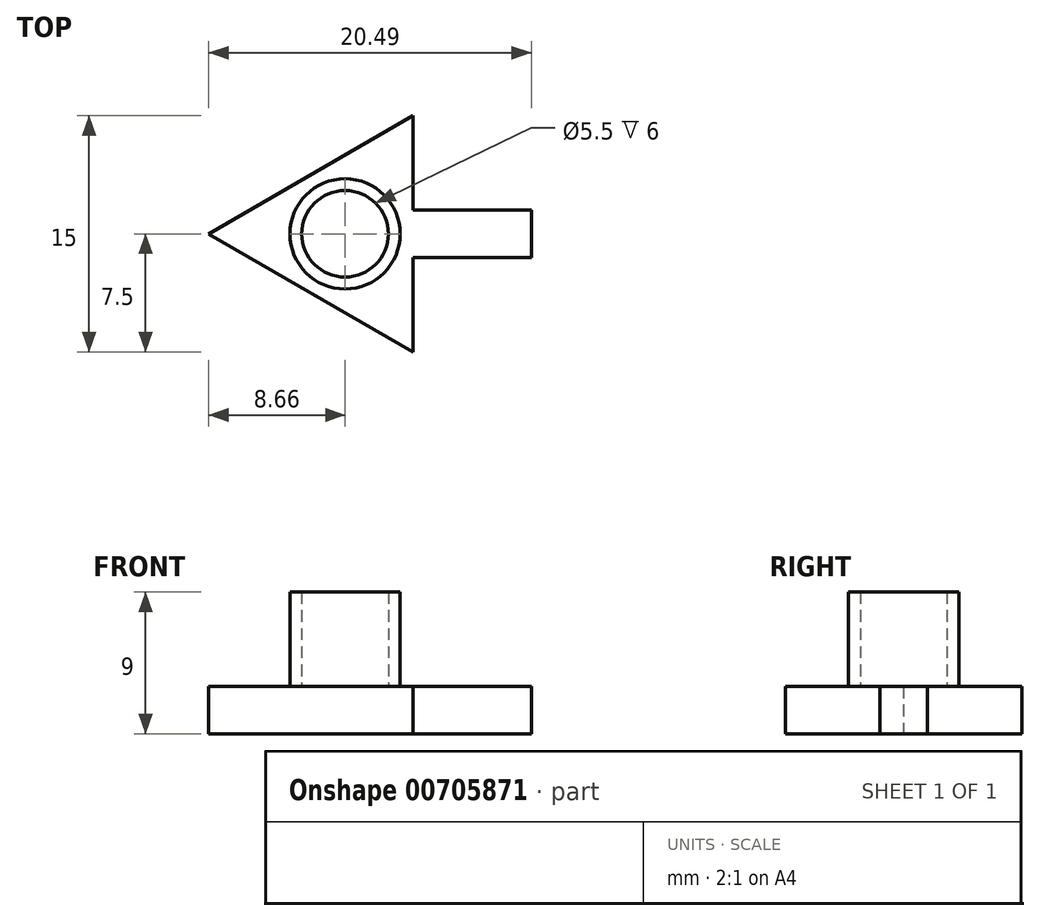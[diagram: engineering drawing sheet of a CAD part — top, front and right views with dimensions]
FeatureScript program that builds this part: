
annotation { "Feature Type Name" : "Feature", "Feature Type Description" : "" }
export const myFeature = defineFeature(function(context is Context, id is Id, definition is map)
    precondition{}
    {
        {
            var Q0;
            Q0=qCreatedBy(makeId("Top.planeOp"),FACE);
            var sketch = newSketch(context, id + "F0", { "sketchPlane" : qUnion([Q0])});
            skCircle(sketch, "E0.cCircle", {"center": v(0, 0) * mm, "radius": 4.33 * mm, "construction": true});
            skLineSegment(sketch, "E0.0", {"start": v(4.33, 7.5) * mm, "end": v(4.33, -7.5) * mm});
            skLineSegment(sketch, "E0.1", {"start": v(4.33, -7.5) * mm, "end": v(-8.66, 0) * mm});
            skLineSegment(sketch, "E0.2", {"start": v(-8.66, 0) * mm, "end": v(4.33, 7.5) * mm});
            skPoint(sketch, "E0.0.midPoint", {"position": v(4.33, 0) * mm});
            skLineSegment(sketch, "E1.bottom", {"start": v(11.83, 1.5) * mm, "end": v(-3.17, 1.5) * mm});
            skLineSegment(sketch, "E1.top", {"start": v(11.83, -1.5) * mm, "end": v(-3.17, -1.5) * mm});
            skLineSegment(sketch, "E1.left", {"start": v(11.83, 1.5) * mm, "end": v(11.83, -1.5) * mm});
            skLineSegment(sketch, "E1.right", {"start": v(-3.17, 1.5) * mm, "end": v(-3.17, -1.5) * mm});
            skSolve(sketch);
        }
        {
            var Q0;
            Q0 = qSketchRegion(id + "F0", true);
            extrude(context, id + "F1", {"entities" : qUnion([Q0]), "depth" : 3 * mm, "offsetDistance" : 25 * mm});
        }
        {
            var Q0;
            Q0=makeQuery(id+"F1.opExtrude","CAP_FACE",FACE,{"disambiguationData":[OSD([sQuery(id+"F0.wireOp",EDGE,"E0.0"),sQuery(id+"F0.wireOp",EDGE,"E0.1"),sQuery(id+"F0.wireOp",EDGE,"E0.2"),sQuery(id+"F0.wireOp",EDGE,"E1.bottom"),sQuery(id+"F0.wireOp",EDGE,"E1.top"),sQuery(id+"F0.wireOp",EDGE,"E1.left")])],"isStart":false});
            var sketch = newSketch(context, id + "F2", { "sketchPlane" : qUnion([Q0])});
            skCircle(sketch, "E2", {"center": v(0, 0) * mm, "radius": 3.5 * mm});
            skCircle(sketch, "E3", {"center": v(0, 0) * mm, "radius": 2.75 * mm});
            skSolve(sketch);
        }
        {
            var Q0;
            Q0=makeQuery(id+"F2.imprint","IMPRINT",FACE,{"disambiguationData":[TD([[makeQuery(id+"F2.imprint","IMPRINT",EDGE,{"derivedFrom":sQuery(id+"F2.wireOp",EDGE,"E2")}),1.0]])]});
            extrude(context, id + "F3", {"entities" : qUnion([Q0]), "operationType" : NewBodyOperationType.ADD, "depth" : 6 * mm, "offsetDistance" : 25 * mm});
        }
    });
